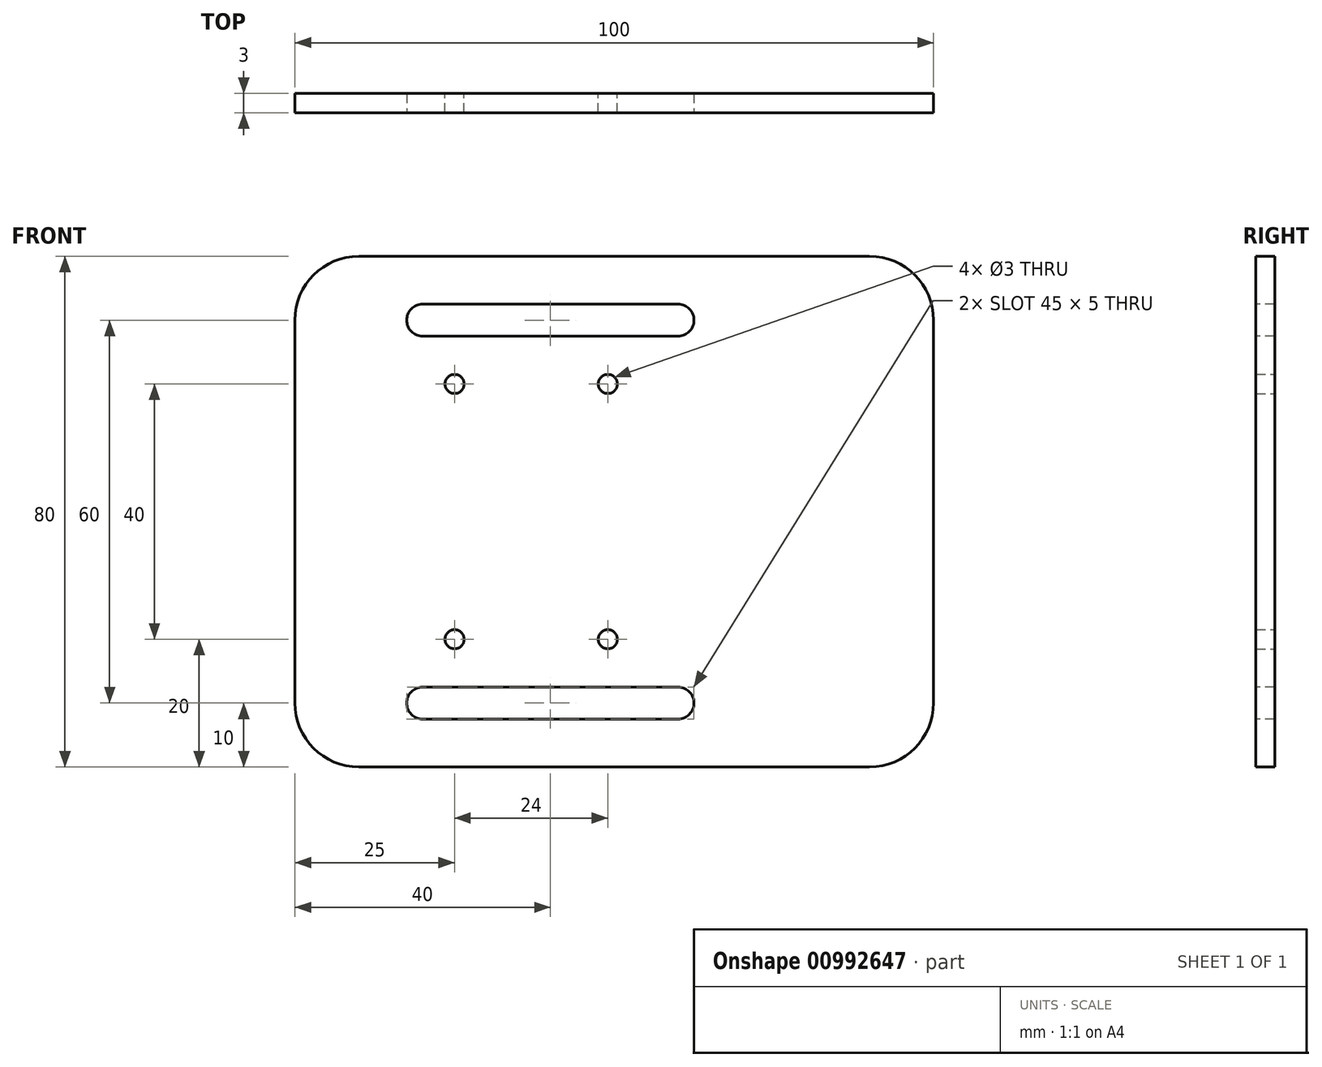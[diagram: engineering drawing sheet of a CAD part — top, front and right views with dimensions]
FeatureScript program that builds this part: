
annotation { "Feature Type Name" : "Feature", "Feature Type Description" : "" }
export const myFeature = defineFeature(function(context is Context, id is Id, definition is map)
    precondition{}
    {
        {
            var Q0;
            Q0=qCreatedBy(makeId("Front.planeOp"),FACE);
            var sketch = newSketch(context, id + "F0", { "sketchPlane" : qUnion([Q0])});
            skLineSegment(sketch, "E0.bottom", {"start": v(0, 0) * mm, "end": v(-100, 0) * mm});
            skLineSegment(sketch, "E0.top", {"start": v(0, -40) * mm, "end": v(-100, -40) * mm});
            skLineSegment(sketch, "E0.left", {"start": v(0, 0) * mm, "end": v(0, -40) * mm});
            skLineSegment(sketch, "E0.right", {"start": v(-100, 0) * mm, "end": v(-100, -40) * mm});
            skSolve(sketch);
        }
        {
            var Q0;
            Q0 = qSketchRegion(id + "F0", true);
            extrude(context, id + "F1", {"entities" : qUnion([Q0]), "depth" : 3 * mm, "offsetDistance" : 25 * mm});
        }
        {
            var Q0;
            Q0=qCreatedBy(makeId("Front.planeOp"),FACE);
            var sketch = newSketch(context, id + "F2", { "sketchPlane" : qUnion([Q0])});
            skLineSegment(sketch, "E1", {"start": v(-75, -20) * mm, "end": v(-51, -20) * mm});
            skLineSegment(sketch, "E2", {"start": v(-51, -20) * mm, "end": v(-75, -20) * mm});
            skSolve(sketch);
        }
        {
            var Q0;
            Q0=sQuery(id+"F2.wireOp",VERTEX,"E2.start");
            var Q1;
            Q1=sQuery(id+"F2.wireOp",VERTEX,"E1.start");
            var Q2;
            Q2=makeQuery(id+"F1.opExtrude","SWEPT_BODY",BODY,{"disambiguationData":[OSD([sQuery(id+"F0.wireOp",EDGE,"E0.bottom"),sQuery(id+"F0.wireOp",EDGE,"E0.top"),sQuery(id+"F0.wireOp",EDGE,"E0.left"),sQuery(id+"F0.wireOp",EDGE,"E0.right")])]});
            hole(context, id + "F3", {"style" : HoleStyle.SIMPLE, "endStyle" : HoleEndStyle.THROUGH, "oppositeDirection" : true, "holeDiameter" : 3 * mm, "majorDiameter" : 5 * mm, "isTappedThrough" : true, "tappedDepth" : 12 * mm, "tapClearance" : 3, "locations" : qUnion([Q0, Q1]), "scope" : qUnion([Q2])});
        }
        {
            var Q0;
            Q0=makeQuery(id+"F1.opExtrude","CAP_FACE",FACE,{"disambiguationData":[OSD([sQuery(id+"F0.wireOp",EDGE,"E0.bottom"),sQuery(id+"F0.wireOp",EDGE,"E0.top"),sQuery(id+"F0.wireOp",EDGE,"E0.left"),sQuery(id+"F0.wireOp",EDGE,"E0.right")])],"isStart":false});
            var sketch = newSketch(context, id + "F4", { "sketchPlane" : qUnion([Q0])});
            skLineSegment(sketch, "E3", {"start": v(-80, -30) * mm, "end": v(-40, -30) * mm});
            skLineSegment(sketch, "E4", {"start": v(-40, -30) * mm, "end": v(-80, -30) * mm});
            skSolve(sketch);
        }
        {
            var Q0;
            {var subQ3=sQuery(id+"F0.wireOp",EDGE,"E0.bottom");Q0=makeQuery(id+"F4.imprint","IMPRINT",FACE,{"disambiguationData":[TD([[makeQuery(id+"F4.imprint","IMPRINT",EDGE,{"derivedFrom":makeQuery(id+"F1.opExtrude","CAP_EDGE",EDGE,{"disambiguationData":[OSD([subQ3])],"isStart":false})}),1.0]])]});}
            var sketch = newSketch(context, id + "F5", { "sketchPlane" : qUnion([Q0])});
            skSolve(sketch);
        }
        {
            var Q0;
            {var subQ3=sQuery(id+"F0.wireOp",EDGE,"E0.bottom");Q0=makeQuery(id+"F5.imprint","IMPRINT",FACE,{"disambiguationData":[TD([[makeQuery(id+"F5.imprint","IMPRINT",EDGE,{"derivedFrom":makeQuery(id+"F4.imprint","IMPRINT",EDGE,{"derivedFrom":makeQuery(id+"F1.opExtrude","CAP_EDGE",EDGE,{"disambiguationData":[OSD([subQ3])],"isStart":false})})}),1.0]])]});}
            var sketch = newSketch(context, id + "F6", { "sketchPlane" : qUnion([Q0])});
            skLineSegment(sketch, "E5.JTB.JTB", {"start": v(-80, -30) * mm, "end": v(-40, -30) * mm, "construction": true});
            skArc(sketch, "E5.0.startCap", {"start": v(-80, -32.5) * mm, "mid": v(-82.5, -30) * mm, "end": v(-80, -27.5) * mm});
            skArc(sketch, "E5.0.endCap", {"start": v(-40, -27.5) * mm, "mid": v(-37.5, -30) * mm, "end": v(-40, -32.5) * mm});
            skLineSegment(sketch, "E5.0.left", {"start": v(-80, -27.5) * mm, "end": v(-40, -27.5) * mm});
            skLineSegment(sketch, "E5.0.right", {"start": v(-80, -32.5) * mm, "end": v(-40, -32.5) * mm});
            skSolve(sketch);
        }
        {
            var Q0;
            Q0 = qSketchRegion(id + "F6", true);
            extrude(context, id + "F7", {"entities" : qUnion([Q0]), "operationType" : NewBodyOperationType.REMOVE, "oppositeDirection" : true, "depth" : 25 * mm, "offsetDistance" : 25 * mm});
        }
        {
            var Q0;
            Q0=makeQuery(id+"F1.opExtrude","SWEPT_EDGE",EDGE,{"disambiguationData":[OSD([sQuery(id+"F0.wireOp",EDGE,"E0.top"),sQuery(id+"F0.wireOp",EDGE,"E0.right")])]});
            var Q1;
            Q1=makeQuery(id+"F1.opExtrude","SWEPT_EDGE",EDGE,{"disambiguationData":[OSD([sQuery(id+"F0.wireOp",EDGE,"E0.top"),sQuery(id+"F0.wireOp",EDGE,"E0.left")])]});
            fillet(context, id + "F8", {"entities" : qUnion([Q0, Q1]), "radius" : 10 * mm, "tangentPropagation" : true, "allowEdgeOverflow" : false});
        }
        {
            var Q0;
            Q0=makeQuery(id+"F1.opExtrude","SWEPT_BODY",BODY,{"disambiguationData":[OSD([sQuery(id+"F0.wireOp",EDGE,"E0.bottom"),sQuery(id+"F0.wireOp",EDGE,"E0.top"),sQuery(id+"F0.wireOp",EDGE,"E0.left"),sQuery(id+"F0.wireOp",EDGE,"E0.right")])]});
            var Q1;
            Q1=qCreatedBy(makeId("Top.planeOp"),FACE);
            mirror(context, id + "F9", {"operationType" : NewBodyOperationType.ADD, "entities" : qUnion([Q0]), "mirrorPlane" : qUnion([Q1])});
        }
    });
